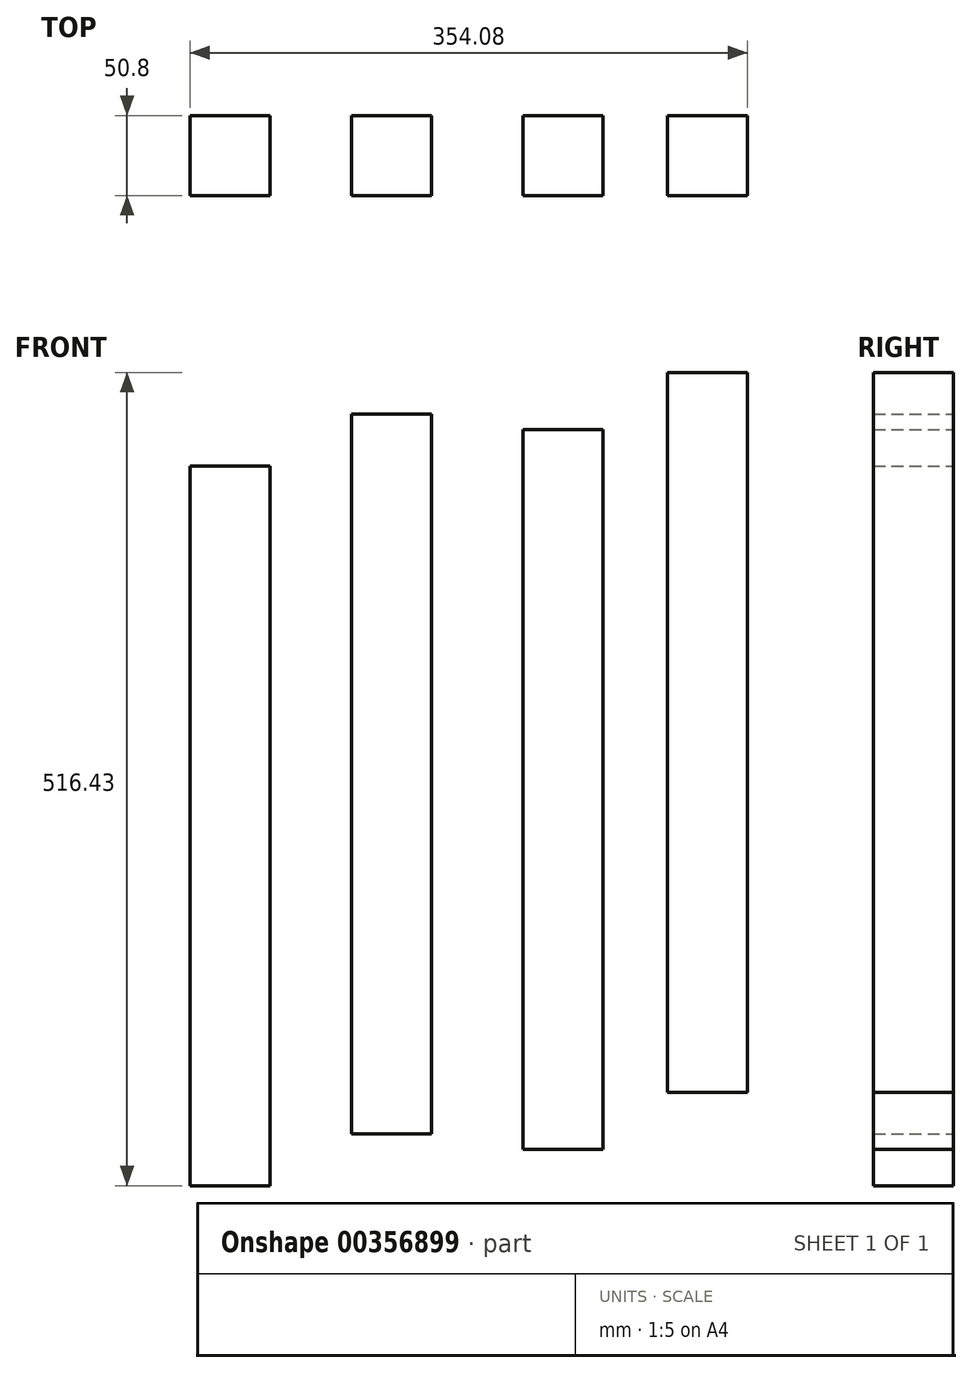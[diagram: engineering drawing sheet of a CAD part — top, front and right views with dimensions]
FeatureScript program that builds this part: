
annotation { "Feature Type Name" : "Feature", "Feature Type Description" : "" }
export const myFeature = defineFeature(function(context is Context, id is Id, definition is map)
    precondition{}
    {
        {
            var Q0;
            Q0=qCreatedBy(makeId("Front.planeOp"),FACE);
            var sketch = newSketch(context, id + "F0", { "sketchPlane" : qUnion([Q0])});
            skLineSegment(sketch, "E0.bottom", {"start": v(-243.45, 241.8) * mm, "end": v(-192.65, 241.8) * mm});
            skLineSegment(sketch, "E0.top", {"start": v(-243.45, -215.4) * mm, "end": v(-192.65, -215.4) * mm});
            skLineSegment(sketch, "E0.left", {"start": v(-243.45, 241.8) * mm, "end": v(-243.45, -215.4) * mm});
            skLineSegment(sketch, "E0.right", {"start": v(-192.65, 241.8) * mm, "end": v(-192.65, -215.4) * mm});
            skLineSegment(sketch, "E1.bottom", {"start": v(-140.86, 274.7) * mm, "end": v(-90.06, 274.7) * mm});
            skLineSegment(sketch, "E1.top", {"start": v(-140.86, -182.5) * mm, "end": v(-90.06, -182.5) * mm});
            skLineSegment(sketch, "E1.left", {"start": v(-140.86, 274.7) * mm, "end": v(-140.86, -182.5) * mm});
            skLineSegment(sketch, "E1.right", {"start": v(-90.06, 274.7) * mm, "end": v(-90.06, -182.5) * mm});
            skLineSegment(sketch, "E2.bottom", {"start": v(-31.89, 264.71) * mm, "end": v(18.91, 264.71) * mm});
            skLineSegment(sketch, "E2.top", {"start": v(-31.89, -192.49) * mm, "end": v(18.91, -192.49) * mm});
            skLineSegment(sketch, "E2.left", {"start": v(-31.89, 264.71) * mm, "end": v(-31.89, -192.49) * mm});
            skLineSegment(sketch, "E2.right", {"start": v(18.91, 264.71) * mm, "end": v(18.91, -192.49) * mm});
            skLineSegment(sketch, "E3.bottom", {"start": v(59.83, 301.03) * mm, "end": v(110.63, 301.03) * mm});
            skLineSegment(sketch, "E3.top", {"start": v(59.83, -156.17) * mm, "end": v(110.63, -156.17) * mm});
            skLineSegment(sketch, "E3.left", {"start": v(59.83, 301.03) * mm, "end": v(59.83, -156.17) * mm});
            skLineSegment(sketch, "E3.right", {"start": v(110.63, 301.03) * mm, "end": v(110.63, -156.17) * mm});
            skSolve(sketch);
        }
        {
            var Q0;
            Q0 = qSketchRegion(id + "F0", true);
            extrude(context, id + "F1", {"entities" : qUnion([Q0]), "depth" : 50.8 * mm});
        }
    });
